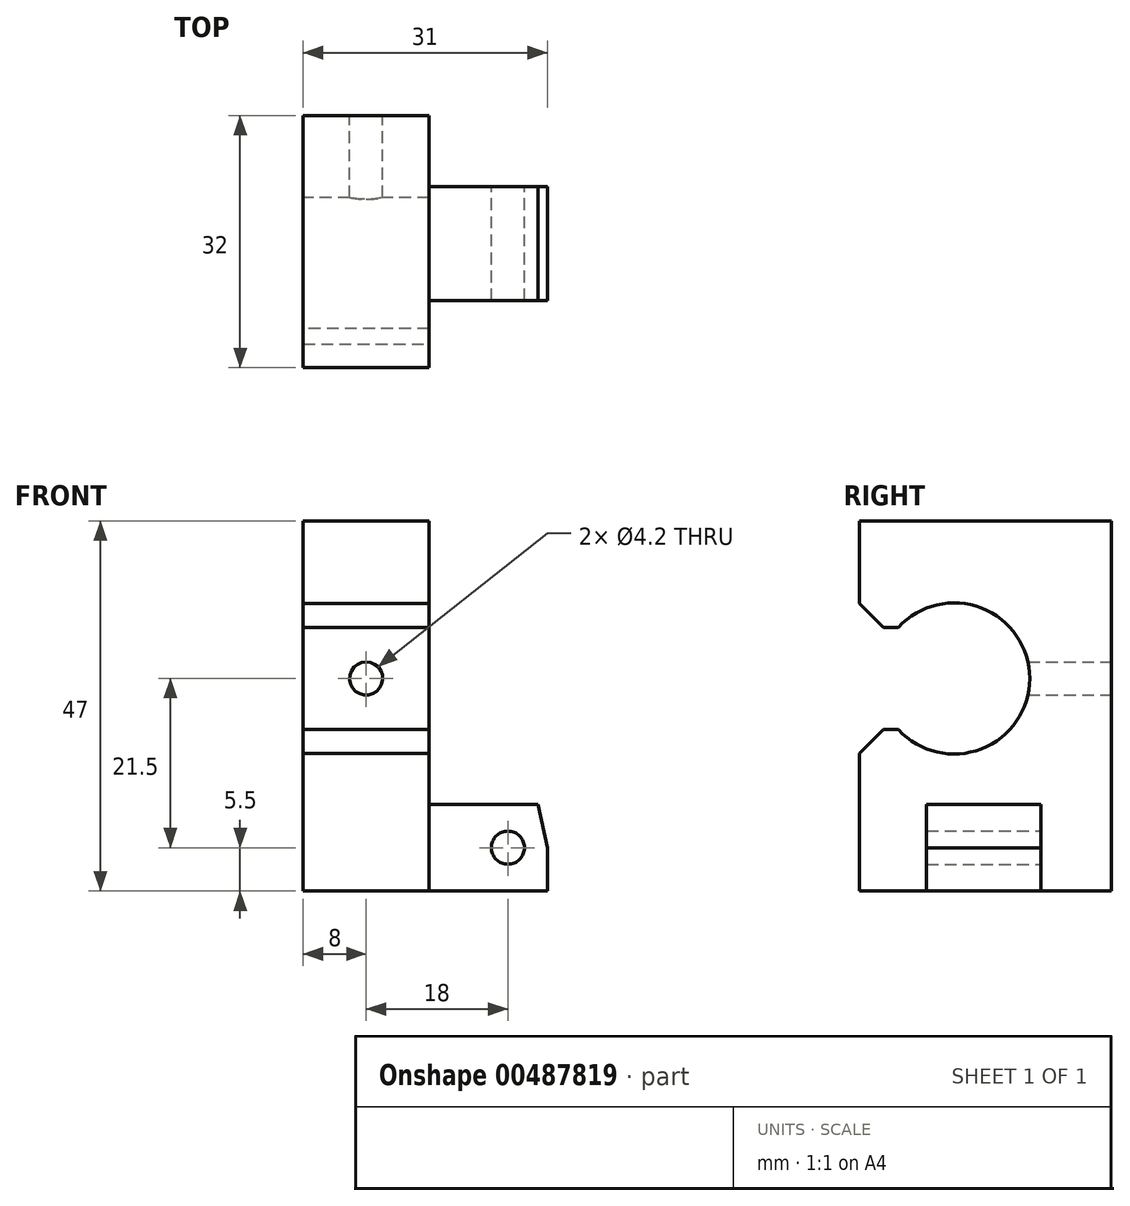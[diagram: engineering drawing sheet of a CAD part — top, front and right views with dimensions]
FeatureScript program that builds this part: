
annotation { "Feature Type Name" : "Feature", "Feature Type Description" : "" }
export const myFeature = defineFeature(function(context is Context, id is Id, definition is map)
    precondition{}
    {
        {
            var Q0;
            Q0=qCreatedBy(makeId("Right.planeOp"),FACE);
            var sketch = newSketch(context, id + "F0", { "sketchPlane" : qUnion([Q0])});
            skArc(sketch, "E0", {"start": v(-7.06, -6.5) * mm, "mid": v(9.6, 0) * mm, "end": v(-7.06, 6.5) * mm});
            skLineSegment(sketch, "E1.bottom", {"start": v(-12, 20) * mm, "end": v(20, 20) * mm});
            skLineSegment(sketch, "E1.top", {"start": v(-12, -27) * mm, "end": v(20, -27) * mm});
            skLineSegment(sketch, "E1.left", {"start": v(-12, 20) * mm, "end": v(-12, -27) * mm});
            skLineSegment(sketch, "E1.right", {"start": v(20, 20) * mm, "end": v(20, -27) * mm});
            skLineSegment(sketch, "E2.bottom", {"start": v(-7.06, 6.5) * mm, "end": v(-12, 6.5) * mm});
            skLineSegment(sketch, "E2.top", {"start": v(-7.06, -6.5) * mm, "end": v(-12, -6.5) * mm});
            skPoint(sketch, "E3.orphan", {"position": v(20, 6.5) * mm});
            skPoint(sketch, "E4.orphan", {"position": v(20, -6.5) * mm});
            skPoint(sketch, "E2.right.start.orphan", {"position": v(-20, 6.5) * mm});
            skPoint(sketch, "E5.orphan", {"position": v(-20, -6.5) * mm});
            skSolve(sketch);
        }
        {
            var Q0;
            Q0=makeQuery(id+"F0.imprint","IMPRINT",FACE,{"disambiguationData":[TD([[makeQuery(id+"F0.imprint","IMPRINT",EDGE,{"derivedFrom":sQuery(id+"F0.wireOp",EDGE,"E0")}),-1.0]])]});
            extrude(context, id + "F1", {"entities" : qUnion([Q0]), "depth" : 16 * mm, "offsetDistance" : 25 * mm});
        }
        {
            var Q0;
            Q0=makeQuery(id+"F1.opExtrude","CAP_FACE",FACE,{"disambiguationData":[OSD([sQuery(id+"F0.wireOp",EDGE,"E0"),sQuery(id+"F0.wireOp",EDGE,"E1.bottom"),sQuery(id+"F0.wireOp",EDGE,"E1.top"),sQuery(id+"F0.wireOp",EDGE,"E1.left"),sQuery(id+"F0.wireOp",EDGE,"E1.right")])],"isStart":false});
            var sketch = newSketch(context, id + "F2", { "sketchPlane" : qUnion([Q0])});
            skLineSegment(sketch, "E6.bottom", {"start": v(11, -27) * mm, "end": v(-3.5, -27) * mm});
            skLineSegment(sketch, "E6.top", {"start": v(11, -16) * mm, "end": v(-3.5, -16) * mm});
            skLineSegment(sketch, "E6.left", {"start": v(11, -27) * mm, "end": v(11, -16) * mm});
            skLineSegment(sketch, "E6.right", {"start": v(-3.5, -27) * mm, "end": v(-3.5, -16) * mm});
            skSolve(sketch);
        }
        {
            var Q0;
            Q0=makeQuery(id+"F2.imprint","IMPRINT",FACE,{"disambiguationData":[TD([[makeQuery(id+"F2.imprint","IMPRINT",EDGE,{"derivedFrom":sQuery(id+"F2.wireOp",EDGE,"E6.bottom")}),1.0]])]});
            extrude(context, id + "F3", {"entities" : qUnion([Q0]), "operationType" : NewBodyOperationType.ADD, "depth" : 15 * mm, "offsetDistance" : 25 * mm});
        }
        {
            var Q0;
            Q0=makeQuery(id+"F3.opExtrude","SWEPT_FACE",FACE,{"disambiguationData":[OSD([sQuery(id+"F2.wireOp",EDGE,"E6.right")])]});
            var sketch = newSketch(context, id + "F4", { "sketchPlane" : qUnion([Q0])});
            skLineSegment(sketch, "E7", {"start": v(31, -21.5) * mm, "end": v(31, -16) * mm});
            skLineSegment(sketch, "E8", {"start": v(31, -16) * mm, "end": v(29.83, -16) * mm});
            skLineSegment(sketch, "E9", {"start": v(29.83, -16) * mm, "end": v(31, -21.5) * mm});
            skSolve(sketch);
        }
        {
            var Q0;
            Q0=makeQuery(id+"F4.imprint","IMPRINT",FACE,{"disambiguationData":[TD([[makeQuery(id+"F4.imprint","IMPRINT",EDGE,{"derivedFrom":sQuery(id+"F4.wireOp",EDGE,"E7")}),1.0]])]});
            extrude(context, id + "F5", {"entities" : qUnion([Q0]), "operationType" : NewBodyOperationType.REMOVE, "endBound" : BoundingType.THROUGH_ALL, "oppositeDirection" : true, "depth" : 25 * mm, "offsetDistance" : 25 * mm});
        }
        {
            var Q0;
            Q0=makeQuery(id+"F3.opExtrude","SWEPT_FACE",FACE,{"disambiguationData":[OSD([sQuery(id+"F2.wireOp",EDGE,"E6.left")])]});
            var sketch = newSketch(context, id + "F6", { "sketchPlane" : qUnion([Q0])});
            skPoint(sketch, "E10", {"position": v(-26, -21.5) * mm});
            skSolve(sketch);
        }
        {
            var Q0;
            Q0=sQuery(id+"F6.wireOp",VERTEX,"E10");
            var Q1;
            Q1=makeQuery(id+"F1.opExtrude","SWEPT_BODY",BODY,{"disambiguationData":[OSD([sQuery(id+"F0.wireOp",EDGE,"E0"),sQuery(id+"F0.wireOp",EDGE,"E1.bottom"),sQuery(id+"F0.wireOp",EDGE,"E1.top"),sQuery(id+"F0.wireOp",EDGE,"E1.left"),sQuery(id+"F0.wireOp",EDGE,"E1.right"),sQuery(id+"F0.wireOp",EDGE,"E2.bottom"),sQuery(id+"F0.wireOp",EDGE,"E2.top")])]});
            hole(context, id + "F7", {"style" : HoleStyle.SIMPLE, "endStyle" : HoleEndStyle.THROUGH, "standardTappedOrClearance" : lookupTablePath({ "standard" : "ISO", "engagement" : "75%", "pitch" : "0.8 mm", "size" : "M5", "type" : "Tapped" }), "standardBlindInLast" : lookupTablePath({ "standard" : "ISO", "engagement" : "75%", "pitch" : "0.8 mm", "size" : "M5", "type" : "Tapped" }), "holeDiameter" : 4.2 * mm, "showTappedDepth" : true, "isTappedThrough" : true, "tappedDepth" : 12 * mm, "tapClearance" : 3, "locations" : qUnion([Q0]), "scope" : qUnion([Q1]), "majorDiameter" : 5 * mm});
        }
        {
            var Q0;
            Q0=makeQuery(id+"F1.opExtrude","SWEPT_FACE",FACE,{"disambiguationData":[OSD([sQuery(id+"F0.wireOp",EDGE,"E1.right")])]});
            var sketch = newSketch(context, id + "F8", { "sketchPlane" : qUnion([Q0])});
            skPoint(sketch, "E11", {"position": v(-8, 0) * mm});
            skSolve(sketch);
        }
        {
            var Q0;
            Q0=sQuery(id+"F8.wireOp",VERTEX,"E11");
            var Q1;
            Q1=makeQuery(id+"F1.opExtrude","SWEPT_BODY",BODY,{"disambiguationData":[OSD([sQuery(id+"F0.wireOp",EDGE,"E0"),sQuery(id+"F0.wireOp",EDGE,"E1.bottom"),sQuery(id+"F0.wireOp",EDGE,"E1.top"),sQuery(id+"F0.wireOp",EDGE,"E1.left"),sQuery(id+"F0.wireOp",EDGE,"E1.right"),sQuery(id+"F0.wireOp",EDGE,"E2.bottom"),sQuery(id+"F0.wireOp",EDGE,"E2.top")])]});
            hole(context, id + "F9", {"style" : HoleStyle.SIMPLE, "endStyle" : HoleEndStyle.THROUGH, "standardTappedOrClearance" : lookupTablePath({ "standard" : "ISO", "engagement" : "75%", "pitch" : "0.8 mm", "size" : "M5", "type" : "Tapped" }), "standardBlindInLast" : lookupTablePath({ "standard" : "ISO", "fit" : "Normal", "engagement" : "75%", "pitch" : "0.8 mm", "size" : "M5", "type" : "Clearance & tapped" }), "holeDiameter" : 4.2 * mm, "majorDiameter" : 5 * mm, "showTappedDepth" : true, "isTappedThrough" : true, "tappedDepth" : 12 * mm, "tapClearance" : 3, "locations" : qUnion([Q0]), "scope" : qUnion([Q1])});
        }
        {
            var Q0;
            Q0=makeQuery(id+"F1.opExtrude","SWEPT_EDGE",EDGE,{"disambiguationData":[OSD([sQuery(id+"F0.wireOp",EDGE,"E1.left"),sQuery(id+"F0.wireOp",EDGE,"E2.bottom")])]});
            var Q1;
            Q1=makeQuery(id+"F1.opExtrude","SWEPT_EDGE",EDGE,{"disambiguationData":[OSD([sQuery(id+"F0.wireOp",EDGE,"E1.left"),sQuery(id+"F0.wireOp",EDGE,"E2.top")])]});
            chamfer(context, id + "F10", {"entities" : qUnion([Q0, Q1]), "width" : 3 * mm, "tangentPropagation" : true});
        }
    });
